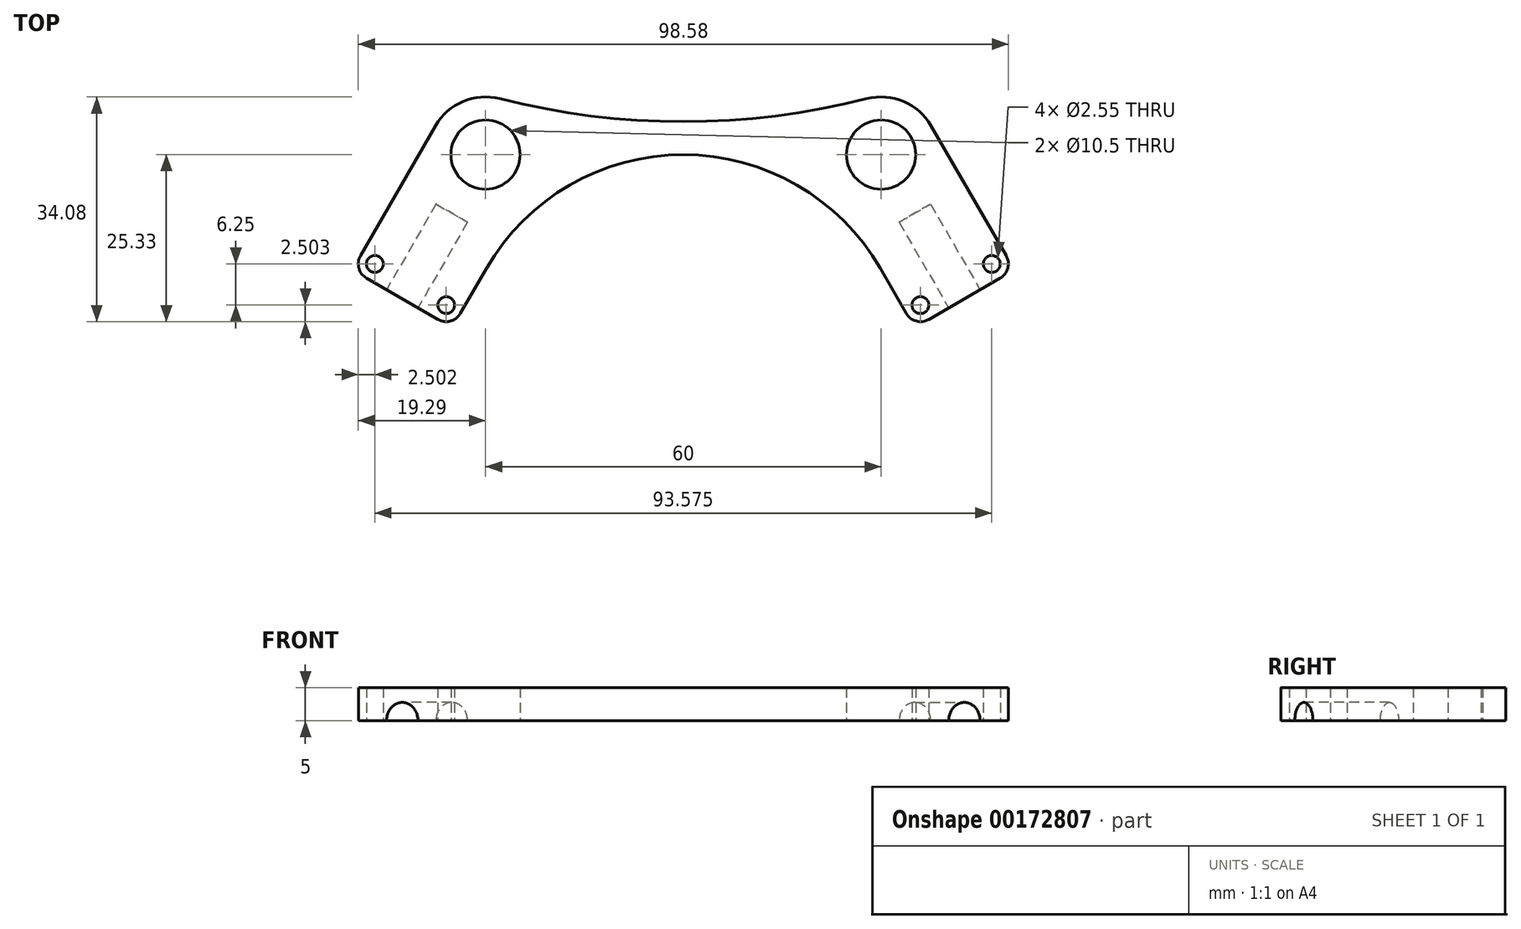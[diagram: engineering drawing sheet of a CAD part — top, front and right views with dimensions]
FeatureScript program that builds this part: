
annotation { "Feature Type Name" : "Feature", "Feature Type Description" : "" }
export const myFeature = defineFeature(function(context is Context, id is Id, definition is map)
    precondition{}
    {
        {
            var Q0;
            Q0=qCreatedBy(makeId("Top.planeOp"),FACE);
            var sketch = newSketch(context, id + "F0", { "sketchPlane" : qUnion([Q0])});
            skCircle(sketch, "E0", {"center": v(-30, 0) * mm, "radius": 5.25 * mm});
            skCircle(sketch, "E1", {"center": v(30, 0) * mm, "radius": 5.25 * mm});
            skLineSegment(sketch, "E2", {"start": v(-30, 0) * mm, "end": v(30, 0) * mm, "construction": true});
            skArc(sketch, "E3", {"start": v(-27.85, 8.48) * mm, "mid": v(-33.4, 8.06) * mm, "end": v(-37.58, 4.37) * mm});
            skArc(sketch, "E4", {"start": v(37.58, 4.38) * mm, "mid": v(33.4, 8.06) * mm, "end": v(27.85, 8.48) * mm});
            skLineSegment(sketch, "E5", {"start": v(-37.58, 4.38) * mm, "end": v(-50.2, -17.5) * mm});
            skLineSegment(sketch, "E6", {"start": v(-50.2, -17.5) * mm, "end": v(-35.05, -26.24) * mm});
            skLineSegment(sketch, "E7", {"start": v(-35.05, -26.24) * mm, "end": v(-29.84, -17.23) * mm});
            skLineSegment(sketch, "E8", {"start": v(29.84, -17.23) * mm, "end": v(35.05, -26.24) * mm});
            skLineSegment(sketch, "E9", {"start": v(35.05, -26.24) * mm, "end": v(50.2, -17.5) * mm});
            skLineSegment(sketch, "E10", {"start": v(50.2, -17.5) * mm, "end": v(37.58, 4.38) * mm});
            skArc(sketch, "E11", {"start": v(29.84, -17.23) * mm, "mid": v(0, 0) * mm, "end": v(-29.84, -17.23) * mm});
            skArc(sketch, "E12", {"start": v(-27.85, 8.48) * mm, "mid": v(0, 5) * mm, "end": v(27.85, 8.48) * mm});
            skSolve(sketch);
        }
        {
            var Q0;
            Q0 = qSketchRegion(id + "F0", true);
            extrude(context, id + "F1", {"entities" : qUnion([Q0]), "depth" : 5 * mm});
        }
        {
            var Q0;
            Q0=makeQuery(id+"F1.opExtrude","SWEPT_FACE",FACE,{"disambiguationData":[OSD([sQuery(id+"F0.wireOp",EDGE,"E6")])]});
            var sketch = newSketch(context, id + "F2", { "sketchPlane" : qUnion([Q0])});
            skCircle(sketch, "E13", {"center": v(-25.98, 0) * mm, "radius": 2.75 * mm});
            skSolve(sketch);
        }
        {
            var Q0;
            Q0 = qSketchRegion(id + "F2", true);
            extrude(context, id + "F3", {"entities" : qUnion([Q0]), "operationType" : NewBodyOperationType.REMOVE, "oppositeDirection" : true, "depth" : 15 * mm});
        }
        {
            var Q0;
            Q0=makeQuery(id+"F1.opExtrude","SWEPT_FACE",FACE,{"disambiguationData":[OSD([sQuery(id+"F0.wireOp",EDGE,"E9")])]});
            var sketch = newSketch(context, id + "F4", { "sketchPlane" : qUnion([Q0])});
            skCircle(sketch, "E14", {"center": v(25.98, 0) * mm, "radius": 2.75 * mm});
            skSolve(sketch);
        }
        {
            var Q0;
            Q0 = qSketchRegion(id + "F4", true);
            extrude(context, id + "F5", {"entities" : qUnion([Q0]), "operationType" : NewBodyOperationType.REMOVE, "oppositeDirection" : true, "depth" : 15 * mm});
        }
        {
            var Q0;
            Q0=makeQuery(id+"F1.opExtrude","CAP_FACE",FACE,{"disambiguationData":[OSD([sQuery(id+"F0.wireOp",EDGE,"E0"),sQuery(id+"F0.wireOp",EDGE,"E1"),sQuery(id+"F0.wireOp",EDGE,"E3"),sQuery(id+"F0.wireOp",EDGE,"E4"),sQuery(id+"F0.wireOp",EDGE,"E5"),sQuery(id+"F0.wireOp",EDGE,"E6"),sQuery(id+"F0.wireOp",EDGE,"E7"),sQuery(id+"F0.wireOp",EDGE,"E8"),sQuery(id+"F0.wireOp",EDGE,"E9"),sQuery(id+"F0.wireOp",EDGE,"E10"),sQuery(id+"F0.wireOp",EDGE,"E11"),sQuery(id+"F0.wireOp",EDGE,"E12")])],"isStart":true});
            var sketch = newSketch(context, id + "F6", { "sketchPlane" : qUnion([Q0])});
            skCircle(sketch, "E15", {"center": v(-46.79, 16.58) * mm, "radius": 1.27 * mm});
            skPoint(sketch, "E15.centerSnap0", {"position": v(-36.5, 16.75) * mm});
            skCircle(sketch, "E16", {"center": v(-46.79, 16.58) * mm, "radius": 2.5 * mm, "construction": true});
            skCircle(sketch, "E17", {"center": v(-35.96, 22.83) * mm, "radius": 1.27 * mm});
            skCircle(sketch, "E18", {"center": v(-35.96, 22.83) * mm, "radius": 2.5 * mm, "construction": true});
            skCircle(sketch, "E19", {"center": v(35.96, 22.83) * mm, "radius": 1.27 * mm});
            skCircle(sketch, "E20", {"center": v(35.96, 22.83) * mm, "radius": 2.5 * mm, "construction": true});
            skCircle(sketch, "E21", {"center": v(46.79, 16.58) * mm, "radius": 1.27 * mm});
            skCircle(sketch, "E22", {"center": v(46.79, 16.58) * mm, "radius": 2.5 * mm, "construction": true});
            skSolve(sketch);
        }
        {
            var Q0;
            Q0 = qSketchRegion(id + "F6", true);
            extrude(context, id + "F7", {"entities" : qUnion([Q0]), "operationType" : NewBodyOperationType.REMOVE, "endBound" : BoundingType.THROUGH_ALL, "oppositeDirection" : true, "depth" : 25 * mm});
        }
        {
            var Q0;
            Q0=makeQuery(id+"F1.opExtrude","SWEPT_EDGE",EDGE,{"disambiguationData":[OSD([sQuery(id+"F0.wireOp",EDGE,"E5"),sQuery(id+"F0.wireOp",EDGE,"E6")])]});
            var Q1;
            Q1=makeQuery(id+"F1.opExtrude","SWEPT_EDGE",EDGE,{"disambiguationData":[OSD([sQuery(id+"F0.wireOp",EDGE,"E6"),sQuery(id+"F0.wireOp",EDGE,"E7")])]});
            var Q2;
            Q2=makeQuery(id+"F1.opExtrude","SWEPT_EDGE",EDGE,{"disambiguationData":[OSD([sQuery(id+"F0.wireOp",EDGE,"E8"),sQuery(id+"F0.wireOp",EDGE,"E9")])]});
            var Q3;
            Q3=makeQuery(id+"F1.opExtrude","SWEPT_EDGE",EDGE,{"disambiguationData":[OSD([sQuery(id+"F0.wireOp",EDGE,"E9"),sQuery(id+"F0.wireOp",EDGE,"E10")])]});
            fillet(context, id + "F8", {"entities" : qUnion([Q0, Q1, Q2, Q3]), "radius" : 2.5 * mm, "tangentPropagation" : true, "allowEdgeOverflow" : false});
        }
    });
